# Revit family: Shower-Rainhead-KOHLER-Katalyst-K-34693T_1
name_source: partatom
category: Plumbing Fixtures
units: mm (PartAtom-declared; Revit-internal decimal feet)

## family parameters
Cut with Voids When Loaded = No
Host = Face
OmniClass Number = 23.31.17.00
OmniClass Title = Showers
Part Type = Normal
Room Calculation Point = No
Round Connector Dimension = Use Diameter
Shared = No

## types (3) — shared parameters
ADA Compliant = No
Assembly Code = D2010700
CW Connection = No
Cold Water Inlet = Cold Water Inlet
Date Modified = 05/24/2023
Default Elevation = 42"
Description = Air Rainhead 12 inch Round
Drain Included = No
Flow Rate = 3 GPM
HW Connection = Yes
Height = 2 7/16"
Hot Water Inlet = Hot Water Inlet
Length = 12"
Manufacturer = Kohler Co.
Master Format 2014 = 22 42 23
Master Format 2014 Name = Residential Showers
Material = Premium Metal Construction
Panel Thickness = 0"
Pressure = 80.00 psi
Product Name = Katalyst
Tempered Water Inlet = Tempered Water Inlet
URL = http://www.kohler.com.cn
Vent Connection = No
Waste Connection = No
Waste Water Outlet = Waste Water Outlet
WaterSense Certified = No
Width = 12"

## per-type parameters (varying)
| type | Finish | Model | Type |
| AF-Vibrant French Gold | Kohler-Metal-AF-Vibrant_French_Gold | K-34693T-AF | 1 |
| BL-Matte Black | Kohler-Metal-BL-Matte_Black | K-34693T-BL | 2 |
| BN-Vibrant Brushed Nickel | Kohler-Metal-BN-Vibrant_Brushed_Nickel | K-34693T-BN | 3 |

## geometry (parser evidence)
native form markers: Sweep x6
no freeform markers — native parametric forms only
